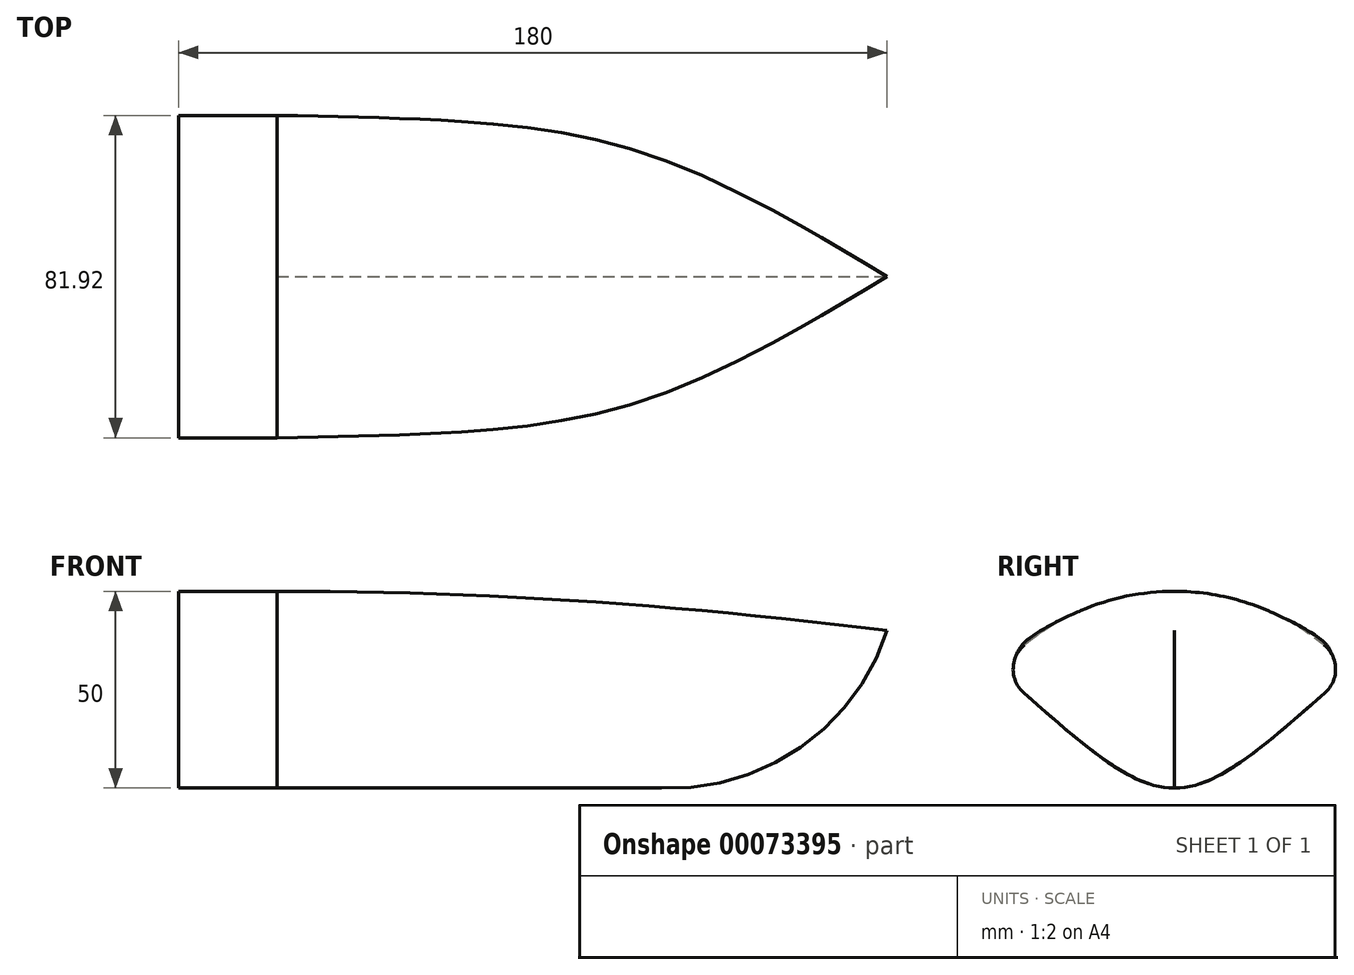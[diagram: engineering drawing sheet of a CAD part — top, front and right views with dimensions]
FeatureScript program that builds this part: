
annotation { "Feature Type Name" : "Feature", "Feature Type Description" : "" }
export const myFeature = defineFeature(function(context is Context, id is Id, definition is map)
    precondition{}
    {
        {
            var Q0;
            Q0=qCreatedBy(makeId("Right.planeOp"),FACE);
            cPlane(context, id + "F0", {"entities" : qUnion([Q0]), "cplaneType" : CPlaneType.OFFSET, "offset" : 180 * mm, "width" : 150 * mm, "height" : 150 * mm});
        }
        {
            var Q0;
            Q0=qCreatedBy(makeId("Right.planeOp"),FACE);
            var sketch = newSketch(context, id + "F1", { "sketchPlane" : qUnion([Q0])});
            skArc(sketch, "E0", {"start": v(44.72, 0) * mm, "mid": v(0, 20) * mm, "end": v(-44.72, 0) * mm});
            skFitSpline(sketch, "E1", {"points": [v(-44.72, 0) * mm, v(44.72, 0) * mm], "startDerivative": vector(134.16, -120) * mm, "endDerivative": vector(134.16, 120) * mm});
            skArc(sketch, "E2", {"start": v(-38.03, 6.4) * mm, "mid": v(-40.96, 0.38) * mm, "end": v(-38.27, -5.76) * mm});
            skLineSegment(sketch, "E3", {"start": v(0, 20) * mm, "end": v(0, 0) * mm, "construction": true});
            skArc(sketch, "E4.0.MirrorCS", {"start": v(38.03, 6.4) * mm, "mid": v(40.96, 0.38) * mm, "end": v(38.27, -5.76) * mm});
            skSolve(sketch);
        }
        {
            var Q0;
            {var subQ1=sQuery(id+"F1.wireOp",EDGE,"E2");Q0=makeQuery(id+"F1.imprint","IMPRINT",FACE,{"disambiguationData":[TD([[makeQuery(id+"F1.imprint","IMPRINT",EDGE,{"derivedFrom":subQ1}),1.0]])]});}
            extrude(context, id + "F2", {"entities" : qUnion([Q0]), "depth" : 25 * mm});
        }
        {
            var Q0;
            Q0=qCreatedBy(id+"F0.planeOp",FACE);
            var sketch = newSketch(context, id + "F3", { "sketchPlane" : qUnion([Q0])});
            skPoint(sketch, "E5", {"position": v(0, 10) * mm});
            skSolve(sketch);
        }
        {
            var Q0;
            Q0=makeQuery(id+"F2.opExtrude","CAP_VERTEX",VERTEX,{"disambiguationData":[OSD([sQuery(id+"F1.wireOp",EDGE,"E0"),sQuery(id+"F1.wireOp",EDGE,"E4.0.MirrorCS")])],"isStart":false});
            var Q1;
            Q1=makeQuery(id+"F2.opExtrude","CAP_VERTEX",VERTEX,{"disambiguationData":[OSD([sQuery(id+"F1.wireOp",EDGE,"E0"),sQuery(id+"F1.wireOp",EDGE,"E2")])],"isStart":false});
            var Q2;
            Q2=sQuery(id+"F3.wireOp",VERTEX,"E5");
            cPlane(context, id + "F4", {"entities" : qUnion([Q0, Q1, Q2]), "cplaneType" : CPlaneType.THREE_POINT, "offset" : 150 * mm, "width" : 150 * mm, "height" : 150 * mm});
        }
        {
            var Q0;
            Q0=qCreatedBy(id+"F4.planeOp",FACE);
            var sketch = newSketch(context, id + "F5", { "sketchPlane" : qUnion([Q0])});
            skFitSpline(sketch, "E6", {"points": [v(25.14, -38.03) * mm, v(180.18, 0) * mm], "startDerivative": vector(240, 0) * mm, "endDerivative": vector(193.93, 114.08) * mm});
            skLineSegment(sketch, "E7", {"start": v(105.14, -38.03) * mm, "end": v(115.54, -38.03) * mm, "construction": true});
            skLineSegment(sketch, "E8", {"start": v(180.18, 0) * mm, "end": v(148.05, 0) * mm, "construction": true});
            skFitSpline(sketch, "E9.0.MirrorCS", {"points": [v(25.14, 38.03) * mm, v(180.18, 0) * mm], "startDerivative": vector(240, 0) * mm, "endDerivative": vector(193.93, -114.08) * mm});
            skSolve(sketch);
        }
        {
            var Q0;
            Q0=qCreatedBy(makeId("Front.planeOp"),FACE);
            var sketch = newSketch(context, id + "F6", { "sketchPlane" : qUnion([Q0])});
            skFitSpline(sketch, "E10", {"points": [v(25, 20) * mm, v(180, 10) * mm], "startDerivative": vector(60, 0) * mm, "endDerivative": vector(238.12, -30) * mm});
            skLineSegment(sketch, "E11.0", {"start": v(25, 20) * mm, "end": v(25, 6.4) * mm});
            skSolve(sketch);
        }
        {
            var Q0;
            Q0=qCreatedBy(makeId("Front.planeOp"),FACE);
            var sketch = newSketch(context, id + "F7", { "sketchPlane" : qUnion([Q0])});
            skFitSpline(sketch, "E12", {"points": [v(25, -30) * mm, v(180, 10) * mm], "startDerivative": vector(300, 0) * mm, "endDerivative": vector(30, 120) * mm, "construction": true});
            skLineSegment(sketch, "E13", {"start": v(25, -30) * mm, "end": v(125, -30) * mm});
            skArc(sketch, "E14", {"start": v(125, -30) * mm, "mid": v(159, -18.94) * mm, "end": v(180, 10) * mm});
            skSolve(sketch);
        }
        {
            var Q1;
            Q1=makeQuery(id+"F2.opExtrude","CAP_FACE",FACE,{"disambiguationData":[OSD([sQuery(id+"F1.wireOp",EDGE,"E0"),sQuery(id+"F1.wireOp",EDGE,"E1"),sQuery(id+"F1.wireOp",EDGE,"E2"),sQuery(id+"F1.wireOp",EDGE,"E4.0.MirrorCS")])],"isStart":false});
            var Q2;
            Q2=sQuery(id+"F3.wireOp",VERTEX,"E5");
            var Q3;
            Q3=sQuery(id+"F5.wireOp",EDGE,"E9.0.MirrorCS");
            var Q4;
            Q4=sQuery(id+"F5.wireOp",EDGE,"E6");
            var Q5;
            Q5=sQuery(id+"F6.wireOp",EDGE,"E10");
            var Q6;
            Q6=qConstructionFilter(qBodyType(qCreatedBy(id+"F7",EDGE),BodyType.WIRE),ConstructionObject.NO);
            loft(context, id + "F8", {"operationType" : NewBodyOperationType.ADD, "addGuides" : true, "sheetProfilesArray" : [{ "sheetProfileEntities" : qUnion([Q1]) }, { "sheetProfileEntities" : qUnion([Q2]) }], "guidesArray" : [{ "guideEntities" : qUnion([Q3]), "guideDerivativeType" : LoftGuideDerivativeType.DEFAULT, "guideDerivativeMagnitude" : 1 }, { "guideEntities" : qUnion([Q4]), "guideDerivativeType" : LoftGuideDerivativeType.DEFAULT, "guideDerivativeMagnitude" : 1 }, { "guideEntities" : qUnion([Q5]), "guideDerivativeType" : LoftGuideDerivativeType.DEFAULT, "guideDerivativeMagnitude" : 1 }, { "guideEntities" : qUnion([Q6]), "guideDerivativeType" : LoftGuideDerivativeType.DEFAULT, "guideDerivativeMagnitude" : 1 }]});
        }
    });
